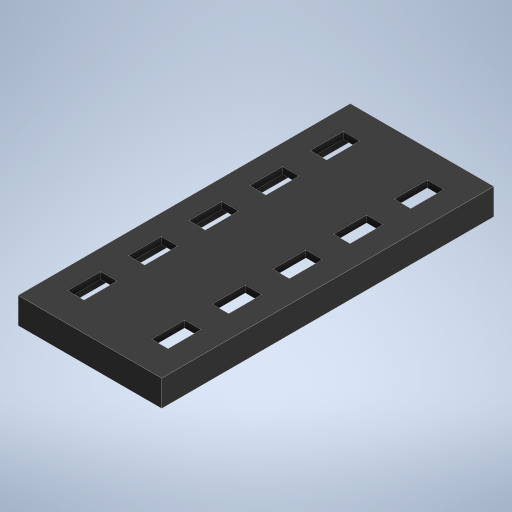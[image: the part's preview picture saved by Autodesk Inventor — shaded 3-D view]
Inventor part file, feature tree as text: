
AUTODESK INVENTOR PART (.ipt)
format: ipt  version: 2024 (Build 280153000, 153)  size: 338,944 bytes
history: native  units: in
note: dims shown in document units (in); Inventor stores cm internally (conversion verified against a paired STEP export)
features: extrude x2, sketch x2, projected_geometry x2
ambient origin geometry x8: Origin, YZ Plane, XZ Plane, XY Plane, X Axis, Y Axis, Z Axis, Center Point
bodies: Body1 (feature_tree)
feature tree (6):
  extrude  "Extrusion4"  Depth=5.753in
  extrude  "Extrusion5"  Depth=0.125in
  sketch  "Sketch4"  dims[d503=2.353in d504=5.753in]
  sketch  "Sketch5"  dims[d505=0.247in d506=0.377in d507=0.3in d508=0.6in d509=0.5in d510=0.3in d511=0.6in d512=0.5in d513=0.3in d514=0.6in d515=0.5in d516=0.3in d517=0.6in d518=0.5in d519=0.3in d520=0.6in d521=0.282in d522=0.377in d523=0.125in d524=0.0in d526=0.35in d527=0.0in d529=0.125in d530=0.02in d531=0.125in d532=0.125in]
  projected_geometry  "Projected Loop2"
  projected_geometry  "Projected Loop3"
